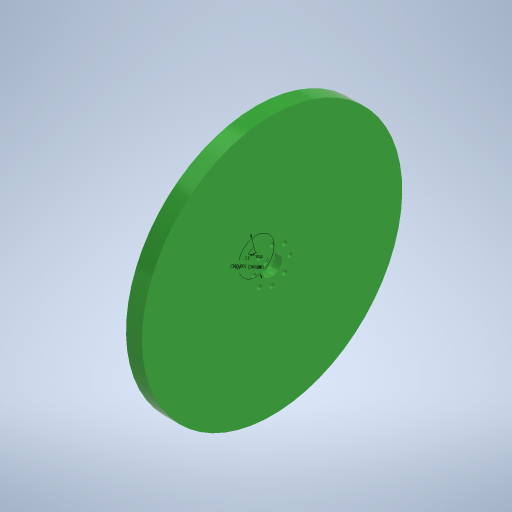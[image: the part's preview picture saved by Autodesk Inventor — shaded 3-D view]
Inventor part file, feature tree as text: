
AUTODESK INVENTOR PART (.ipt)
format: ipt  version: 2024.2 (Build 282272000, 272)  size: 291,328 bytes
history: native  units: mm
features: other x2, sketch x2, extrude x2, revolve x1, fillet x1
ambient origin geometry x8: Origin, YZ Plane, XZ Plane, XY Plane, X Axis, Y Axis, Z Axis, Center Point
bodies: Body1 (feature_tree)
feature tree (8):
  other  "Bryła1"
  revolve  "Obrót1"
  sketch  "Szkic2"
  extrude  "Wyciągnięcie proste1"  Depth=6.0mm
  extrude  "Wyciągnięcie proste2"  Depth=4.1mm
  fillet  "Zaokrąglenie1"  Radius=1.0mm
  sketch  "Szkic1"
  other  "Finish1"
